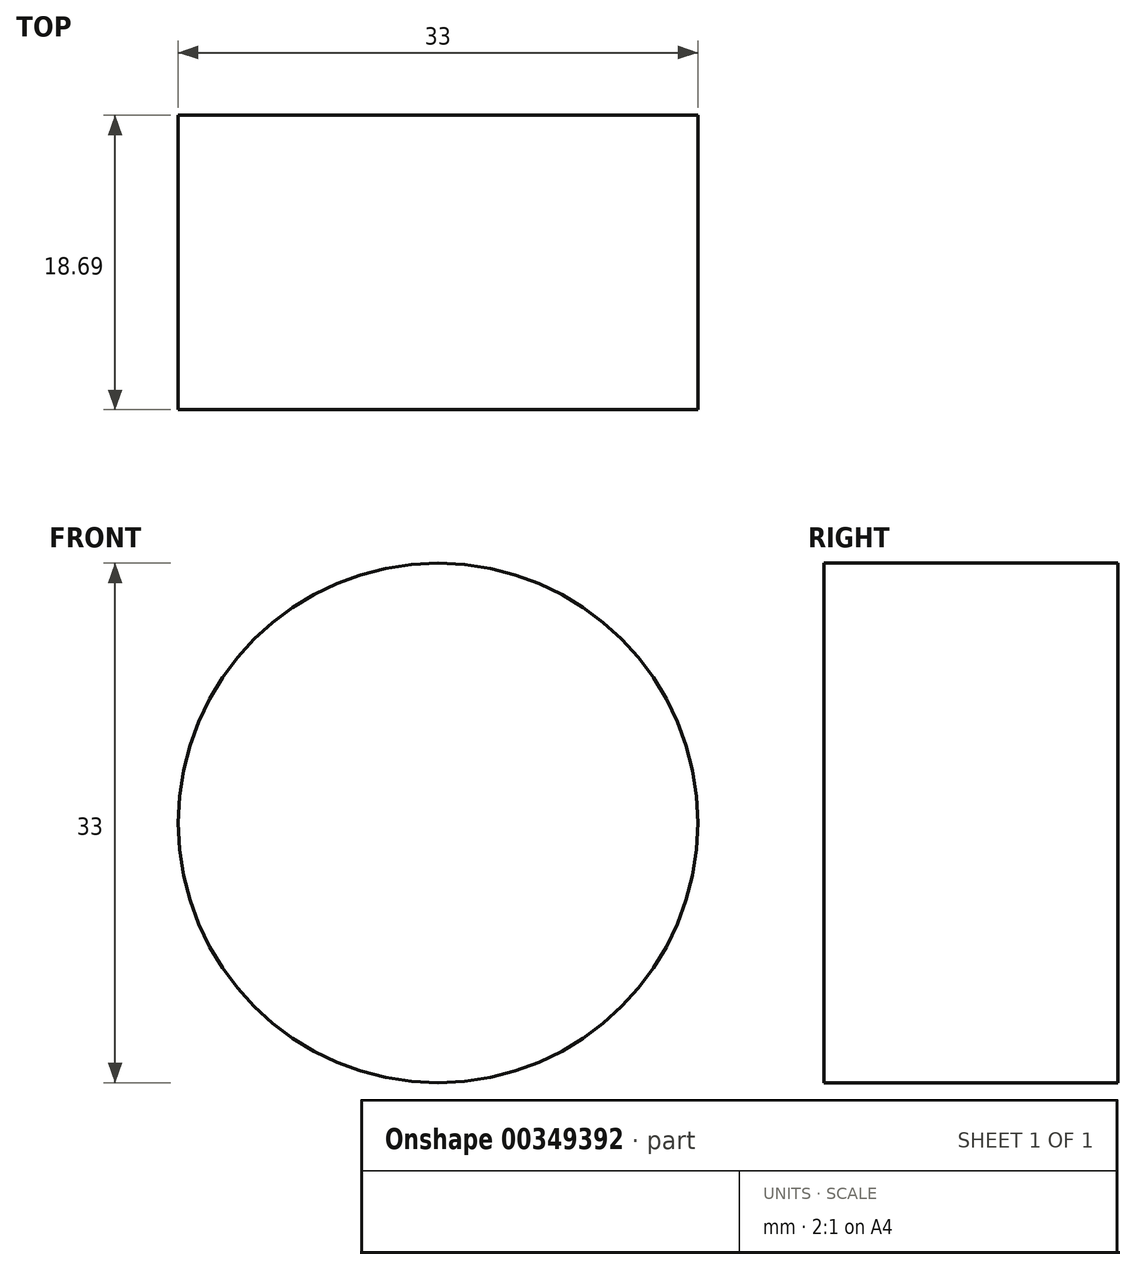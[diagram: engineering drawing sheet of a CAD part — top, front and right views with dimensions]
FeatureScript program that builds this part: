
annotation { "Feature Type Name" : "Feature", "Feature Type Description" : "" }
export const myFeature = defineFeature(function(context is Context, id is Id, definition is map)
    precondition{}
    {
        {
            var Q0;
            Q0=qCreatedBy(makeId("Front.planeOp"),FACE);
            var sketch = newSketch(context, id + "F0", { "sketchPlane" : qUnion([Q0])});
            skCircle(sketch, "E0", {"center": v(0, 0) * mm, "radius": 16.5 * mm});
            skSolve(sketch);
        }
        {
            var Q0;
            Q0 = qSketchRegion(id + "F0", true);
            extrude(context, id + "F1", {"entities" : qUnion([Q0]), "depth" : 18.7 * mm, "offsetDistance" : 25 * mm});
        }
    });
